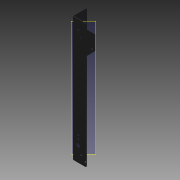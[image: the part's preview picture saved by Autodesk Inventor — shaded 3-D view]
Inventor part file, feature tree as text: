
AUTODESK INVENTOR PART (.ipt)
format: ipt  version: 2015 (Build 190159000, 159)  size: 303,616 bytes
history: native  units: mm
features: extrude x3, other x2, hole x1, plane x1, imported_body x1
ambient origin geometry x8: Origin, YZ Plane, XZ Plane, XY Plane, X Axis, Y Axis, Z Axis, Center Point
bodies: Solid1 (feature_tree)
feature tree (8):
  other  "C04H030039-right-corner-metal-sheet.ipt"
  hole  "Agujero1"  [1 undecoded]
  extrude  "Extrusión2"  Depth=25.0mm
  extrude  "Extrusión6"  Depth=306.5mm
  extrude  "Extrusión7"  Depth=45.0mm
  plane  "Plano de trabajo1"
  imported_body  "DerivedBody::C04H030039-right-corner-metal-sheet.ipt"
  other  "Definición1"
note: 1 required parameter value undecoded (feature->parameter linkage not recoverable at this tier; creation-order binding heuristic only, values carry confidence <= 0.55)
